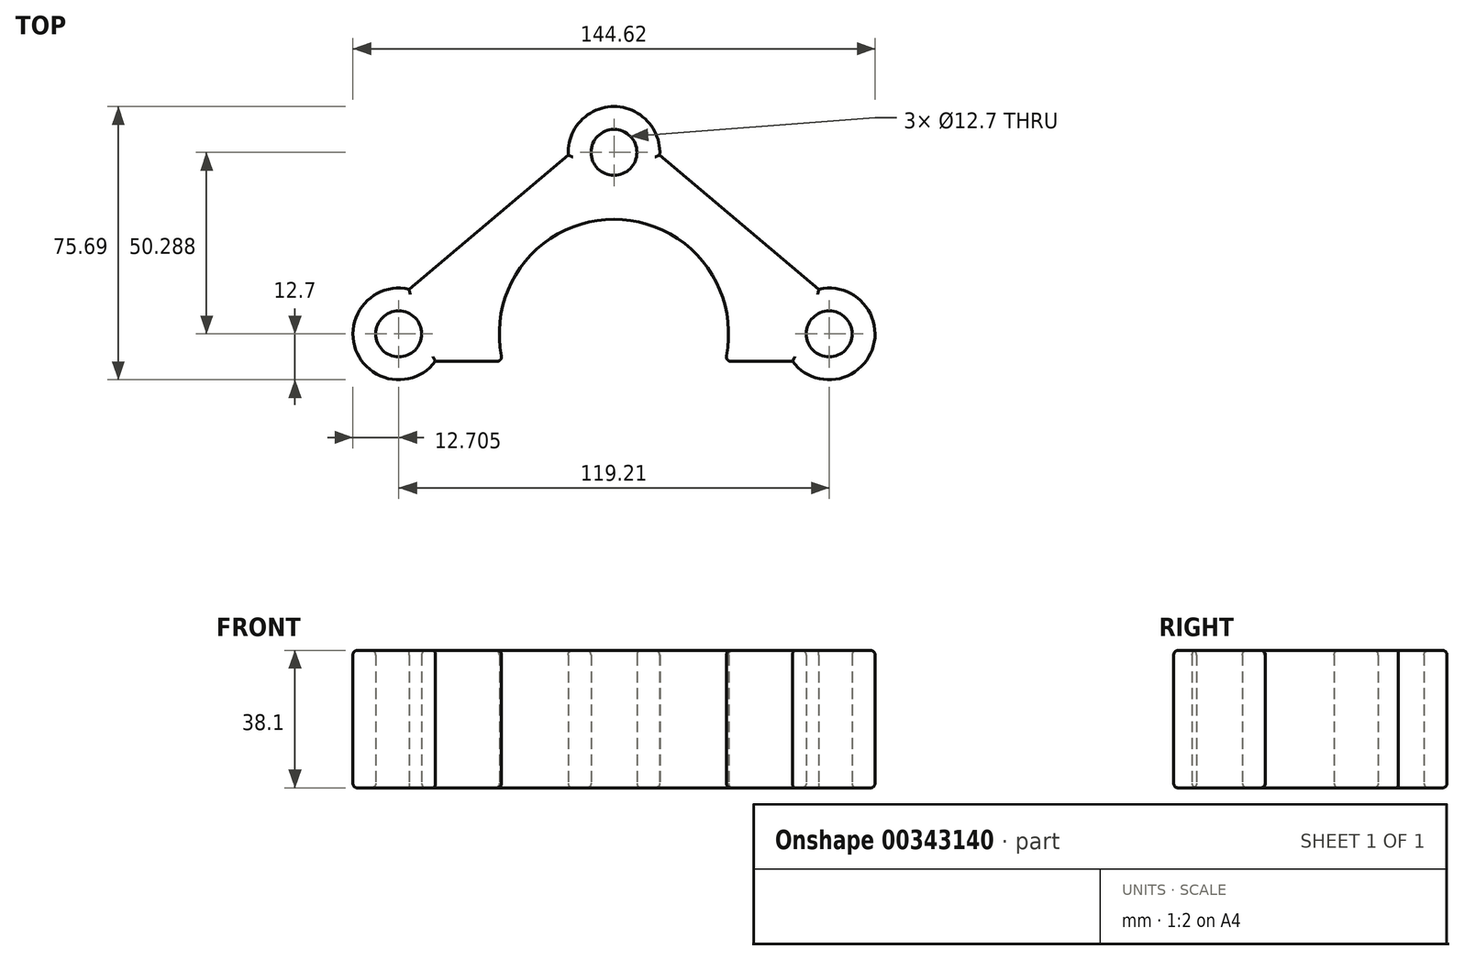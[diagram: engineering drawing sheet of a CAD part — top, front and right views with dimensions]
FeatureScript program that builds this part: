
annotation { "Feature Type Name" : "Feature", "Feature Type Description" : "" }
export const myFeature = defineFeature(function(context is Context, id is Id, definition is map)
    precondition{}
    {
        {
            var Q0;
            Q0=qCreatedBy(makeId("Top.planeOp"),FACE);
            var sketch = newSketch(context, id + "F0", { "sketchPlane" : qUnion([Q0])});
            skCircle(sketch, "E0", {"center": v(0, 50.29) * mm, "radius": 6.35 * mm});
            skCircle(sketch, "E1", {"center": v(59.6, 0) * mm, "radius": 6.35 * mm});
            skCircle(sketch, "E2", {"center": v(-59.6, 0) * mm, "radius": 6.35 * mm});
            skLineSegment(sketch, "E3", {"start": v(0, 50.29) * mm, "end": v(-59.6, 0) * mm, "construction": true});
            skLineSegment(sketch, "E4", {"start": v(59.6, 0) * mm, "end": v(0, 50.29) * mm, "construction": true});
            skLineSegment(sketch, "E5", {"start": v(-59.6, 0) * mm, "end": v(59.6, 0) * mm, "construction": true});
            skPoint(sketch, "E6.visualSharp", {"position": v(0, 66.9) * mm});
            skArc(sketch, "E6.filletArc", {"start": v(12.68, 49.56) * mm, "mid": v(0, 62.99) * mm, "end": v(-12.68, 49.56) * mm});
            skPoint(sketch, "E7.visualSharp", {"position": v(-94.35, -12.7) * mm});
            skArc(sketch, "E7.filletArc", {"start": v(-56.75, 12.38) * mm, "mid": v(-71.53, -4.36) * mm, "end": v(-49.45, -7.62) * mm});
            skPoint(sketch, "E8.visualSharp", {"position": v(94.35, -12.7) * mm});
            skArc(sketch, "E8.filletArc", {"start": v(49.45, -7.62) * mm, "mid": v(71.53, -4.36) * mm, "end": v(56.75, 12.38) * mm});
            skArc(sketch, "E9", {"start": v(31.16, -6.1) * mm, "mid": v(0, 31.75) * mm, "end": v(-31.16, -6.1) * mm});
            skLineSegment(sketch, "E10.0", {"start": v(-12.68, 49.56) * mm, "end": v(-56.75, 12.38) * mm});
            skLineSegment(sketch, "E10.1", {"start": v(56.75, 12.38) * mm, "end": v(12.68, 49.56) * mm});
            skLineSegment(sketch, "E11.0", {"start": v(-49.45, -7.62) * mm, "end": v(-32.4, -7.62) * mm});
            skLineSegment(sketch, "E12.trimOffspring", {"start": v(32.4, -7.62) * mm, "end": v(49.45, -7.62) * mm});
            skPoint(sketch, "E13.visualSharp", {"position": v(-30.82, -7.62) * mm});
            skArc(sketch, "E13.filletArc", {"start": v(-32.4, -7.62) * mm, "mid": v(-31.42, -7.16) * mm, "end": v(-31.16, -6.1) * mm});
            skPoint(sketch, "E14.visualSharp", {"position": v(30.82, -7.62) * mm});
            skArc(sketch, "E14.filletArc", {"start": v(31.16, -6.1) * mm, "mid": v(31.42, -7.16) * mm, "end": v(32.4, -7.62) * mm});
            skSolve(sketch);
        }
        {
            var Q0;
            Q0 = qSketchRegion(id + "F0", true);
            extrude(context, id + "F1", {"entities" : qUnion([Q0]), "depth" : 38.1 * mm});
        }
        {
            var Q0;
            Q0=makeQuery(id+"F1.opExtrude","CAP_FACE",FACE,{"disambiguationData":[OSD([sQuery(id+"F0.wireOp",EDGE,"E0"),sQuery(id+"F0.wireOp",EDGE,"E1"),sQuery(id+"F0.wireOp",EDGE,"E2"),sQuery(id+"F0.wireOp",EDGE,"E6.filletArc"),sQuery(id+"F0.wireOp",EDGE,"E7.filletArc"),sQuery(id+"F0.wireOp",EDGE,"E8.filletArc"),sQuery(id+"F0.wireOp",EDGE,"E9"),sQuery(id+"F0.wireOp",EDGE,"E10.0"),sQuery(id+"F0.wireOp",EDGE,"E10.1"),sQuery(id+"F0.wireOp",EDGE,"E11.0"),sQuery(id+"F0.wireOp",EDGE,"E12.trimOffspring"),sQuery(id+"F0.wireOp",EDGE,"E13.filletArc"),sQuery(id+"F0.wireOp",EDGE,"E14.filletArc")])],"isStart":false});
            fillet(context, id + "F2", {"entities" : qUnion([Q0]), "radius" : 1.27 * mm, "tangentPropagation" : true, "allowEdgeOverflow" : false});
        }
        {
            var Q0;
            Q0=makeQuery(id+"F1.opExtrude","CAP_FACE",FACE,{"disambiguationData":[OSD([sQuery(id+"F0.wireOp",EDGE,"E0"),sQuery(id+"F0.wireOp",EDGE,"E1"),sQuery(id+"F0.wireOp",EDGE,"E2"),sQuery(id+"F0.wireOp",EDGE,"E6.filletArc"),sQuery(id+"F0.wireOp",EDGE,"E7.filletArc"),sQuery(id+"F0.wireOp",EDGE,"E8.filletArc"),sQuery(id+"F0.wireOp",EDGE,"E9"),sQuery(id+"F0.wireOp",EDGE,"E10.0"),sQuery(id+"F0.wireOp",EDGE,"E10.1"),sQuery(id+"F0.wireOp",EDGE,"E11.0"),sQuery(id+"F0.wireOp",EDGE,"E12.trimOffspring"),sQuery(id+"F0.wireOp",EDGE,"E13.filletArc"),sQuery(id+"F0.wireOp",EDGE,"E14.filletArc")])],"isStart":true});
            fillet(context, id + "F3", {"entities" : qUnion([Q0]), "radius" : 1.27 * mm, "tangentPropagation" : true, "allowEdgeOverflow" : false});
        }
    });
